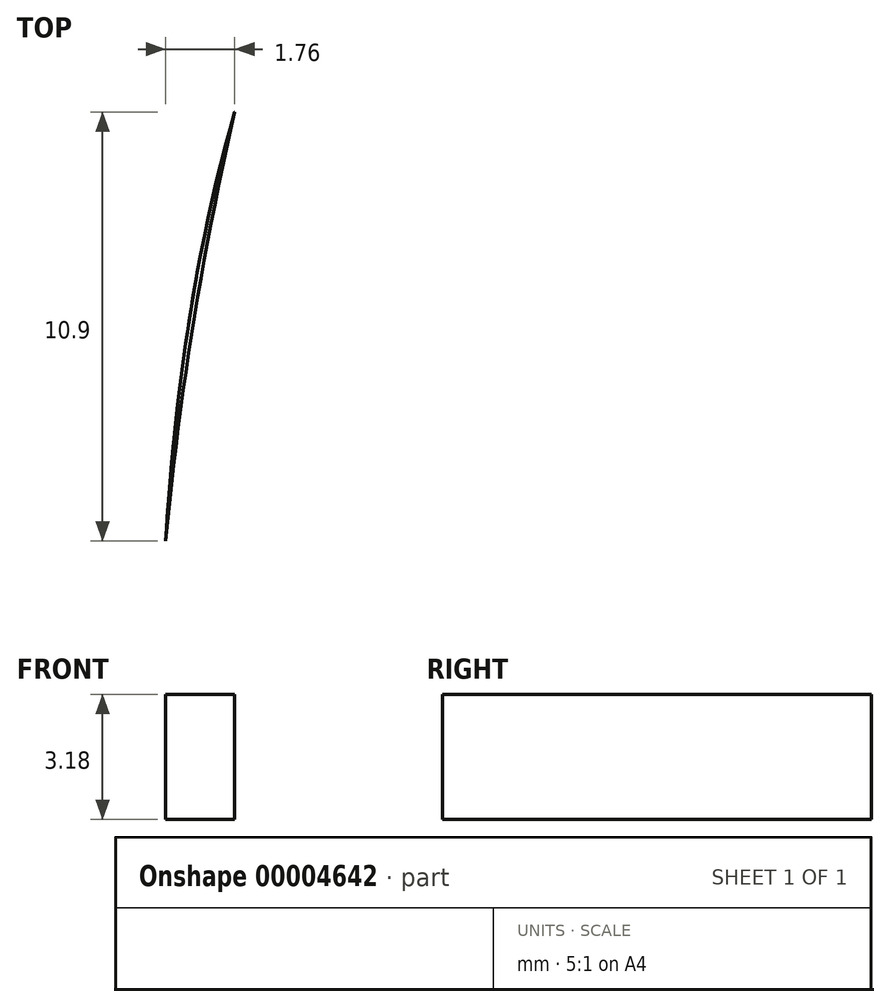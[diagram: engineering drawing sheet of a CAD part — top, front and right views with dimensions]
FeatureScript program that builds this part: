
annotation { "Feature Type Name" : "Feature", "Feature Type Description" : "" }
export const myFeature = defineFeature(function(context is Context, id is Id, definition is map)
    precondition{}
    {
        {
            var Q0;
            Q0=qCreatedBy(makeId("Top.planeOp"),FACE);
            var sketch = newSketch(context, id + "F0", { "sketchPlane" : qUnion([Q0])});
            skLineSegment(sketch, "E0", {"start": v(-1.69, -61.63) * mm, "end": v(33.24, -61.63) * mm});
            skLineSegment(sketch, "E1", {"start": v(61.81, 14.57) * mm, "end": v(61.81, 14.57) * mm});
            skPoint(sketch, "E2", {"position": v(-1.69, -61.63) * mm});
            skLineSegment(sketch, "E3.0.MirrorCS", {"start": v(-1.69, -61.63) * mm, "end": v(-36.61, -61.63) * mm});
            skPoint(sketch, "E4", {"position": v(-65.19, 14.57) * mm});
            skPoint(sketch, "E5.orphan", {"position": v(-65.19, -61.63) * mm});
            skFitSpline(sketch, "E6.0.MirrorCS", {"points": [v(61.81, 14.57) * mm, v(45.03, 7.13) * mm, v(32.1, -26.14) * mm, v(33.24, -61.63) * mm], "startDerivative": vector(-52.15, -19.53) * mm, "endDerivative": vector(3.8, -90.46) * mm});
            skPoint(sketch, "E7.orphan", {"position": v(61.81, -61.63) * mm});
            skLineSegment(sketch, "E8.trimOffspring", {"start": v(61.81, 39.97) * mm, "end": v(61.81, 90.77) * mm});
            skLineSegment(sketch, "E9", {"start": v(-73.21, 90.77) * mm, "end": v(111.84, 90.77) * mm, "construction": true});
            skLineSegment(sketch, "E10", {"start": v(-39.79, 90.77) * mm, "end": v(-39.79, 87.6) * mm});
            skLineSegment(sketch, "E11", {"start": v(-14.39, 87.6) * mm, "end": v(-14.39, 90.77) * mm});
            skLineSegment(sketch, "E12", {"start": v(-14.39, 90.77) * mm, "end": v(-39.79, 90.77) * mm});
            skLineSegment(sketch, "E13.0.MirrorCS", {"start": v(11.01, 87.6) * mm, "end": v(11.01, 90.77) * mm});
            skLineSegment(sketch, "E14.0.MirrorCS", {"start": v(11.01, 90.77) * mm, "end": v(36.41, 90.77) * mm});
            skLineSegment(sketch, "E15.0.MirrorCS", {"start": v(36.41, 90.77) * mm, "end": v(36.41, 87.6) * mm});
            skLineSegment(sketch, "E16.0.MirrorCS", {"start": v(36.41, 87.6) * mm, "end": v(11.01, 87.6) * mm});
            skFitSpline(sketch, "E17.0", {"points": [v(60.47, 18.16) * mm, v(60.01, 17.99) * mm, v(58.98, 17.64) * mm, v(56.56, 16.91) * mm, v(53.7, 16.08) * mm, v(50.63, 14.94) * mm, v(48.25, 13.89) * mm, v(45.85, 12.57) * mm, v(43.9, 11.2) * mm, v(42.37, 9.9) * mm, v(40.91, 8.5) * mm, v(39.24, 6.59) * mm, v(37.42, 4.04) * mm, v(35.8, 1.28) * mm, v(34.33, -1.66) * mm, v(32.6, -5.78) * mm, v(30.82, -11.24) * mm, v(29.52, -16.93) * mm, v(28.76, -21.53) * mm, v(28.34, -24.96) * mm, v(28.05, -28.35) * mm, v(27.84, -32.8) * mm, v(27.85, -38.19) * mm, v(28.16, -44.43) * mm, v(28.78, -52.44) * mm, v(29.25, -58.13) * mm, v(29.4, -61.8) * mm]});
            skFitSpline(sketch, "E18", {"points": [v(-36.61, -61.63) * mm, v(-39.02, -10.55) * mm, v(-65.19, 14.57) * mm], "startDerivative": vector(2.41, 101.96) * mm, "endDerivative": vector(-57.03, 48.48) * mm});
            skFitSpline(sketch, "E19.0.MirrorCS", {"points": [v(33.24, -61.63) * mm, v(35.64, -10.55) * mm, v(61.81, 14.57) * mm], "startDerivative": vector(-2.41, 101.96) * mm, "endDerivative": vector(57.03, 48.48) * mm});
            skLineSegment(sketch, "E20.trimOffspring", {"start": v(33.24, -61.63) * mm, "end": v(33.24, -61.63) * mm});
            skLineSegment(sketch, "E21", {"start": v(-36.16, -57.63) * mm, "end": v(-36.16, -57.63) * mm});
            skLineSegment(sketch, "E22", {"start": v(61.81, 39.97) * mm, "end": v(64.99, 39.97) * mm});
            skLineSegment(sketch, "E23", {"start": v(64.99, 14.57) * mm, "end": v(61.81, 14.57) * mm});
            skLineSegment(sketch, "E24.0.MirrorCS", {"start": v(-65.19, 55.97) * mm, "end": v(-65.19, 90.77) * mm});
            skPoint(sketch, "E25", {"position": v(-33.44, -61.63) * mm});
            skLineSegment(sketch, "E26", {"start": v(-25.69, -57.64) * mm, "end": v(-30.39, -61.63) * mm, "construction": true});
            skLineSegment(sketch, "E27", {"start": v(64.99, 39.97) * mm, "end": v(64.99, 28.01) * mm});
            skArc(sketch, "E28", {"start": v(64.99, 28.01) * mm, "mid": v(61.65, 27.27) * mm, "end": v(64.99, 26.53) * mm});
            skLineSegment(sketch, "E29.trimOffspring", {"start": v(64.99, 26.53) * mm, "end": v(64.99, 14.57) * mm});
            skLineSegment(sketch, "E30", {"start": v(-39.79, 87.6) * mm, "end": v(-14.39, 87.6) * mm});
            skLineSegment(sketch, "E31", {"start": v(-1.69, -61.63) * mm, "end": v(-1.69, 121.52) * mm, "construction": true});
            skPoint(sketch, "E32.start.orphan", {"position": v(-34.7, 46.08) * mm});
            skLineSegment(sketch, "E33", {"start": v(-1.69, -5.24) * mm, "end": v(-31.66, -5.24) * mm});
            skLineSegment(sketch, "E34.0.MirrorCS", {"start": v(-1.69, -5.24) * mm, "end": v(28.28, -5.24) * mm});
            skLineSegment(sketch, "E35", {"start": v(-31.66, -5.24) * mm, "end": v(-31.66, -61.63) * mm});
            skLineSegment(sketch, "E36.0.MirrorCS", {"start": v(28.28, -5.24) * mm, "end": v(28.28, -61.63) * mm});
            skPoint(sketch, "E37.orphan", {"position": v(31.33, 39.45) * mm});
            skPoint(sketch, "E38.orphan", {"position": v(-34.7, 39.45) * mm});
            skArc(sketch, "E39", {"start": v(61.81, 90.77) * mm, "mid": v(-1.69, 110.03) * mm, "end": v(-65.19, 90.77) * mm});
            skLineSegment(sketch, "E40.0.MirrorCS", {"start": v(-68.36, 39.97) * mm, "end": v(-68.36, 28.01) * mm});
            skLineSegment(sketch, "E41.0.MirrorCS", {"start": v(-65.19, 39.97) * mm, "end": v(-68.36, 39.97) * mm});
            skArc(sketch, "E42.0.MirrorCS", {"start": v(-68.36, 28.01) * mm, "mid": v(-65.02, 27.27) * mm, "end": v(-68.36, 26.53) * mm});
            skLineSegment(sketch, "E43.0.MirrorCS", {"start": v(-68.36, 14.57) * mm, "end": v(-65.19, 14.57) * mm});
            skLineSegment(sketch, "E44.0.MirrorCS", {"start": v(-65.19, 39.97) * mm, "end": v(-65.19, 90.77) * mm});
            skLineSegment(sketch, "E45", {"start": v(-68.36, 26.53) * mm, "end": v(-68.36, 14.57) * mm});
            skLineSegment(sketch, "E46", {"start": v(31.33, 46.08) * mm, "end": v(31.33, 54.23) * mm});
            skPoint(sketch, "E47.start.orphan", {"position": v(31.33, 14.78) * mm});
            skPoint(sketch, "E48.start.orphan", {"position": v(31.33, 22.05) * mm});
            skPoint(sketch, "E49.end.orphan", {"position": v(31.33, 29.14) * mm});
            skLineSegment(sketch, "E50", {"start": v(-34.7, 54.23) * mm, "end": v(-34.7, 59.86) * mm});
            skLineSegment(sketch, "E51", {"start": v(31.33, 59.86) * mm, "end": v(31.33, 54.23) * mm});
            skLineSegment(sketch, "E52.trimOffspring", {"start": v(-34.7, 46.08) * mm, "end": v(-34.7, 54.23) * mm});
            skPoint(sketch, "E53.orphan", {"position": v(31.33, 32.28) * mm});
            skPoint(sketch, "E54.orphan", {"position": v(-34.7, 65.5) * mm});
            skPoint(sketch, "E55.orphan", {"position": v(31.33, 65.5) * mm});
            skLineSegment(sketch, "E56", {"start": v(-34.7, 59.86) * mm, "end": v(-34.7, 61.7) * mm});
            skLineSegment(sketch, "E57", {"start": v(31.33, 59.86) * mm, "end": v(31.33, 61.7) * mm});
            skArc(sketch, "E58", {"start": v(31.33, 61.7) * mm, "mid": v(-1.69, 67.46) * mm, "end": v(-34.7, 61.7) * mm});
            skLineSegment(sketch, "E59.0", {"start": v(-34.7, 43.02) * mm, "end": v(31.33, 43.02) * mm});
            skLineSegment(sketch, "E60", {"start": v(-34.7, 43.02) * mm, "end": v(-34.7, 46.08) * mm});
            skLineSegment(sketch, "E61", {"start": v(31.33, 43.02) * mm, "end": v(31.33, 46.08) * mm});
            skSolve(sketch);
        }
        {
            var Q0;
            Q0=makeQuery(id+"F0.imprint","IMPRINT",FACE,{"disambiguationData":[TD([[makeQuery(id+"F0.imprint","IMPRINT",EDGE,{"derivedFrom":sQuery(id+"F0.wireOp",EDGE,"E6.0.MirrorCS")}),-1.0]])]});
            extrude(context, id + "F1", {"entities" : qUnion([Q0]), "depth" : 3.17 * mm});
        }
    });
